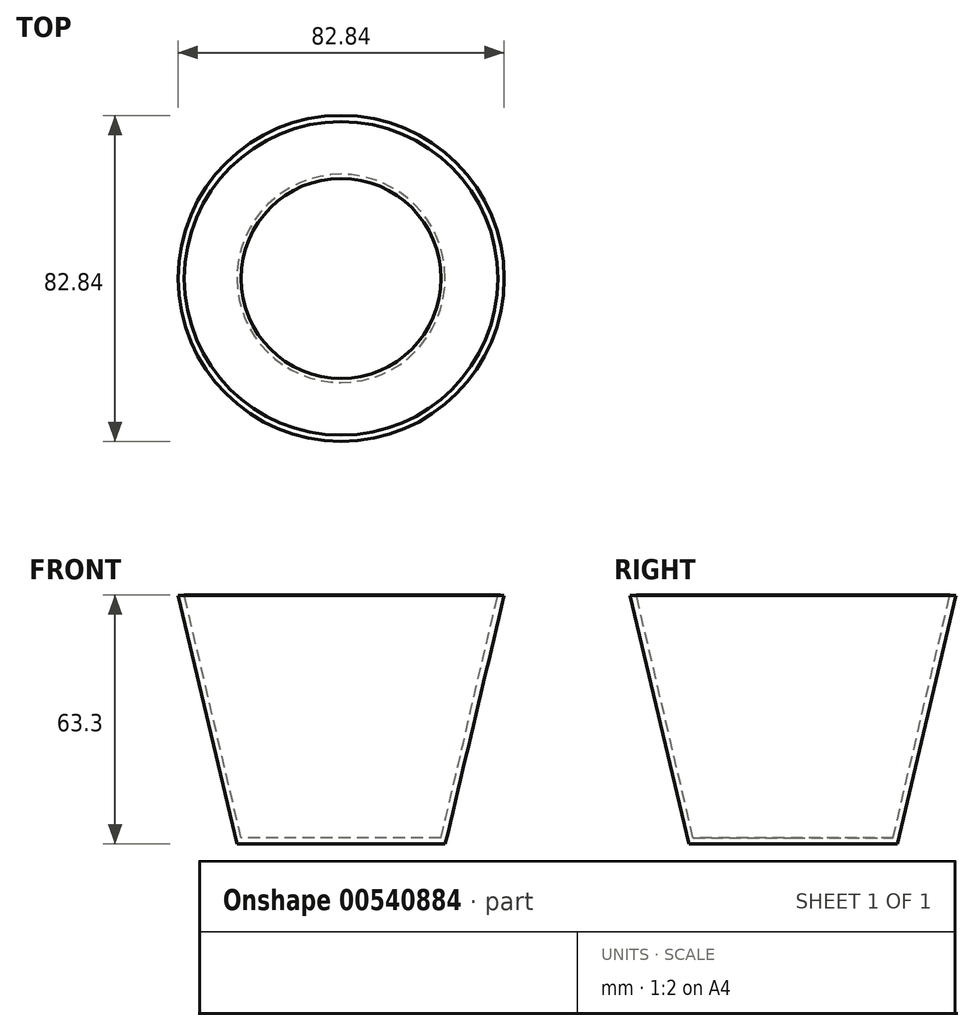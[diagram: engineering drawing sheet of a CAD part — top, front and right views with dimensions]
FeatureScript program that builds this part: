
annotation { "Feature Type Name" : "Feature", "Feature Type Description" : "" }
export const myFeature = defineFeature(function(context is Context, id is Id, definition is map)
    precondition{}
    {
        {
            var Q0;
            Q0=qCreatedBy(makeId("Front.planeOp"),FACE);
            var sketch = newSketch(context, id + "F0", { "sketchPlane" : qUnion([Q0])});
            skLineSegment(sketch, "E0", {"start": v(6.8, 63.13) * mm, "end": v(5.23, 63.3) * mm});
            skLineSegment(sketch, "E1", {"start": v(5.23, 63.3) * mm, "end": v(-9.2, 1.59) * mm});
            skLineSegment(sketch, "E2", {"start": v(-9.2, 1.59) * mm, "end": v(-34.6, 1.59) * mm});
            skLineSegment(sketch, "E3", {"start": v(-34.6, 1.59) * mm, "end": v(-34.6, 0) * mm});
            skLineSegment(sketch, "E4", {"start": v(6.8, 63.13) * mm, "end": v(-8.15, 0) * mm});
            skLineSegment(sketch, "E5", {"start": v(-8.15, 0) * mm, "end": v(-34.6, 0) * mm});
            skSolve(sketch);
        }
        {
            var Q0;
            Q0=makeQuery(id+"F0.imprint","IMPRINT",FACE,{"disambiguationData":[TD([[makeQuery(id+"F0.imprint","IMPRINT",EDGE,{"derivedFrom":sQuery(id+"F0.wireOp",EDGE,"E0")}),1.0]])]});
            var Q1;
            Q1=sQuery(id+"F0.wireOp",EDGE,"E3");
            revolve(context, id + "F1", {"entities" : qUnion([Q0]), "axis" : qUnion([Q1]), "revolveType" : RevolveType.FULL});
        }
    });
